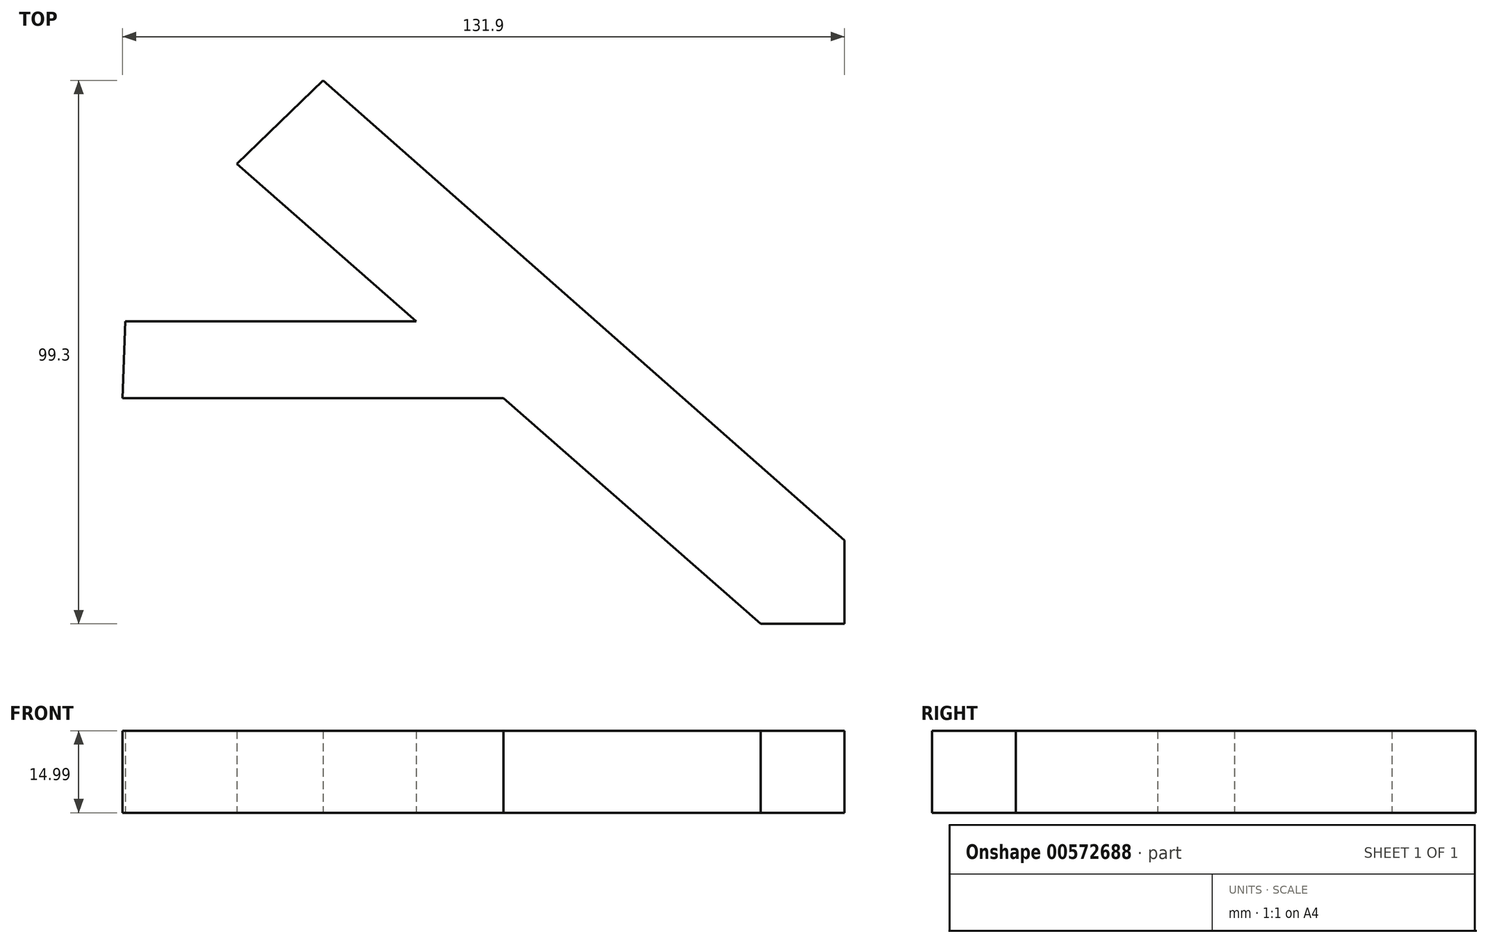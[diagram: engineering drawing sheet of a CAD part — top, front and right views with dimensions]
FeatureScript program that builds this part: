
annotation { "Feature Type Name" : "Feature", "Feature Type Description" : "" }
export const myFeature = defineFeature(function(context is Context, id is Id, definition is map)
    precondition{}
    {
        {
            var Q0;
            Q0=qCreatedBy(makeId("Top.planeOp"),FACE);
            var sketch = newSketch(context, id + "F0", { "sketchPlane" : qUnion([Q0])});
            skLineSegment(sketch, "E0", {"start": v(-37.31, 59.43) * mm, "end": v(57.92, -24.6) * mm});
            skLineSegment(sketch, "E1", {"start": v(57.92, -24.6) * mm, "end": v(57.92, -39.87) * mm});
            skLineSegment(sketch, "E2", {"start": v(57.92, -39.87) * mm, "end": v(42.64, -39.87) * mm});
            skLineSegment(sketch, "E3", {"start": v(42.64, -39.87) * mm, "end": v(-53.1, 44.16) * mm});
            skLineSegment(sketch, "E4", {"start": v(-53.1, 44.16) * mm, "end": v(-37.31, 59.43) * mm});
            skLineSegment(sketch, "E5", {"start": v(-20.33, 15.4) * mm, "end": v(-73.47, 15.4) * mm});
            skLineSegment(sketch, "E6", {"start": v(-73.47, 15.4) * mm, "end": v(-73.98, 1.38) * mm});
            skLineSegment(sketch, "E7", {"start": v(-73.98, 1.38) * mm, "end": v(-4.36, 1.38) * mm});
            skLineSegment(sketch, "E8", {"start": v(-4.36, 1.38) * mm, "end": v(14.88, -15.5) * mm});
            skLineSegment(sketch, "E9", {"start": v(14.88, -15.5) * mm, "end": v(30.11, -28.87) * mm});
            skLineSegment(sketch, "E10", {"start": v(30.11, -28.87) * mm, "end": v(42.64, -39.87) * mm});
            skLineSegment(sketch, "E11", {"start": v(35.68, -33.76) * mm, "end": v(42.64, -39.87) * mm});
            skSolve(sketch);
        }
        {
            var Q0;
            Q0=makeQuery(id+"F0.imprint","IMPRINT",FACE,{"disambiguationData":[TD([[makeQuery(id+"F0.imprint","IMPRINT",EDGE,{"derivedFrom":sQuery(id+"F0.wireOp",EDGE,"E0")}),-1.0]])]});
            var Q1;
            {var subQ2=sQuery(id+"F0.wireOp",EDGE,"E5");Q1=makeQuery(id+"F0.imprint","IMPRINT",FACE,{"disambiguationData":[TD([[makeQuery(id+"F0.imprint","IMPRINT",EDGE,{"derivedFrom":subQ2}),1.0]])]});}
            extrude(context, id + "F1", {"entities" : qUnion([Q0, Q1]), "depth" : 15 * mm, "offsetDistance" : 25.4 * mm});
        }
    });
